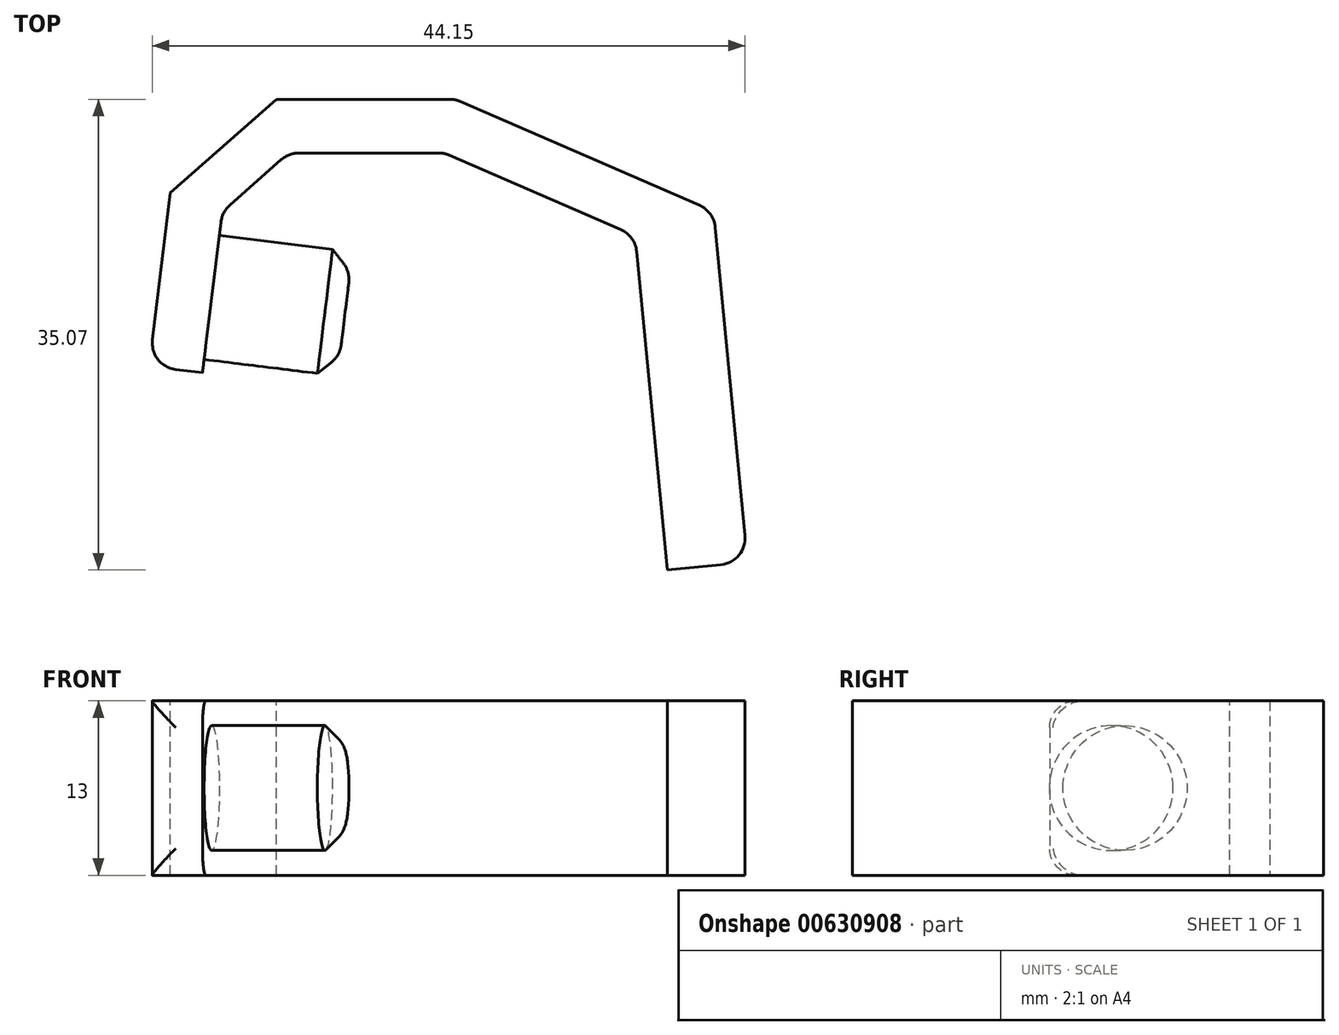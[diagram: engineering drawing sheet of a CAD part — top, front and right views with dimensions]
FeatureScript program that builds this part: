
annotation { "Feature Type Name" : "Feature", "Feature Type Description" : "" }
export const myFeature = defineFeature(function(context is Context, id is Id, definition is map)
    precondition{}
    {
        {
            var Q0;
            Q0=qCreatedBy(makeId("Top.planeOp"),FACE);
            var sketch = newSketch(context, id + "F0", { "sketchPlane" : qUnion([Q0])});
            skLineSegment(sketch, "E0", {"start": v(-44.74, -5.73) * mm, "end": v(-42.73, 10.65) * mm});
            skLineSegment(sketch, "E1", {"start": v(-42.73, 10.65) * mm, "end": v(-26.73, 10.65) * mm});
            skLineSegment(sketch, "E2", {"start": v(-26.73, 10.65) * mm, "end": v(-12.51, 4.47) * mm});
            skLineSegment(sketch, "E3.0", {"start": v(-25.9, 14.65) * mm, "end": v(-6.66, 6.28) * mm});
            skLineSegment(sketch, "E3.1", {"start": v(-46.27, 14.65) * mm, "end": v(-25.9, 14.65) * mm});
            skLineSegment(sketch, "E3.2", {"start": v(-48.7, -5.24) * mm, "end": v(-46.27, 14.65) * mm});
            skLineSegment(sketch, "E4", {"start": v(-48.7, -5.24) * mm, "end": v(-44.74, -5.73) * mm});
            skLineSegment(sketch, "E5", {"start": v(-12.51, 4.47) * mm, "end": v(-10.12, -20.42) * mm});
            skLineSegment(sketch, "E6", {"start": v(-6.66, 6.28) * mm, "end": v(-4.15, -19.84) * mm});
            skLineSegment(sketch, "E7", {"start": v(-4.15, -19.84) * mm, "end": v(-10.12, -20.42) * mm});
            skSolve(sketch);
        }
        {
            var Q0;
            Q0 = qSketchRegion(id + "F0", true);
            extrude(context, id + "F1", {"entities" : qUnion([Q0]), "depth" : 13 * mm, "offsetDistance" : 25 * mm});
        }
        {
            var Q0;
            Q0=makeQuery(id+"F1.opExtrude","SWEPT_FACE",FACE,{"disambiguationData":[OSD([sQuery(id+"F0.wireOp",EDGE,"E0")])]});
            var sketch = newSketch(context, id + "F2", { "sketchPlane" : qUnion([Q0])});
            skCircle(sketch, "E8", {"center": v(-5.5, 6.5) * mm, "radius": 4.65 * mm});
            skSolve(sketch);
        }
        {
            var Q0;
            Q0 = qSketchRegion(id + "F2", true);
            extrude(context, id + "F3", {"entities" : qUnion([Q0]), "operationType" : NewBodyOperationType.ADD, "depth" : 10 * mm, "offsetDistance" : 25 * mm});
        }
        {
            var Q0;
            Q0=makeQuery(id+"F3.opExtrude","CAP_EDGE",EDGE,{"disambiguationData":[OSD([sQuery(id+"F2.wireOp",EDGE,"E8")])],"isStart":false});
            chamfer(context, id + "F4", {"entities" : qUnion([Q0]), "width" : 1.5 * mm, "tangentPropagation" : true});
        }
        {
            var Q0;
            Q0=makeQuery(id+"F1.opExtrude","SWEPT_EDGE",EDGE,{"disambiguationData":[OSD([sQuery(id+"F0.wireOp",EDGE,"E0"),sQuery(id+"F0.wireOp",EDGE,"E1")])]});
            chamfer(context, id + "F5", {"entities" : qUnion([Q0]), "width" : 5 * mm, "tangentPropagation" : true});
        }
        {
            var Q0;
            Q0=makeQuery(id+"F1.opExtrude","CAP_FACE",FACE,{"disambiguationData":[OSD([sQuery(id+"F0.wireOp",EDGE,"E0"),sQuery(id+"F0.wireOp",EDGE,"E1"),sQuery(id+"F0.wireOp",EDGE,"E2"),sQuery(id+"F0.wireOp",EDGE,"E3.0"),sQuery(id+"F0.wireOp",EDGE,"E3.1"),sQuery(id+"F0.wireOp",EDGE,"E3.2"),sQuery(id+"F0.wireOp",EDGE,"E4"),sQuery(id+"F0.wireOp",EDGE,"N3BcXGvI-HXC5-peAH-YZqd-A4wPKsLQrxSF")])],"isStart":false});
            var sketch = newSketch(context, id + "F6", { "sketchPlane" : qUnion([Q0])});
            skLineSegment(sketch, "E9", {"start": v(-47.12, 7.68) * mm, "end": v(-39.24, 14.65) * mm});
            skLineSegment(sketch, "E10", {"start": v(-39.24, 14.65) * mm, "end": v(-43.87, 19.87) * mm});
            skLineSegment(sketch, "E11", {"start": v(-43.87, 19.87) * mm, "end": v(-51.8, 12.85) * mm});
            skLineSegment(sketch, "E12", {"start": v(-51.8, 12.85) * mm, "end": v(-47.12, 7.68) * mm});
            skSolve(sketch);
        }
        {
            var Q0;
            Q0 = qSketchRegion(id + "F6", true);
            extrude(context, id + "F7", {"entities" : qUnion([Q0]), "operationType" : NewBodyOperationType.REMOVE, "oppositeDirection" : true, "depth" : 25 * mm, "offsetDistance" : 25 * mm});
        }
        {
            var Q0;
            Q0=makeQuery(id+"F1.opExtrude","CAP_EDGE",EDGE,{"disambiguationData":[OSD([sQuery(id+"F0.wireOp",EDGE,"E4")])],"isStart":true});
            var Q1;
            Q1=makeQuery(id+"F1.opExtrude","CAP_EDGE",EDGE,{"disambiguationData":[OSD([sQuery(id+"F0.wireOp",EDGE,"E4")])],"isStart":false});
            var Q2;
            Q2=makeQuery(id+"F1.opExtrude","SWEPT_EDGE",EDGE,{"disambiguationData":[OSD([sQuery(id+"F0.wireOp",EDGE,"E6"),sQuery(id+"F0.wireOp",EDGE,"E7")])]});
            var Q3;
            Q3=makeQuery(id+"F3.opExtrude","CAP_EDGE",EDGE,{"disambiguationData":[OSD([sQuery(id+"F2.wireOp",EDGE,"E8")])],"isStart":true});
            var Q4;
            {var subQ0=sQuery(id+"F0.wireOp",EDGE,"E0");Q4=makeQuery(id+"F5.opChamfer","BLEND_EDGE",EDGE,{"blendedFrom":[makeQuery(id+"F1.opExtrude","SWEPT_EDGE",EDGE,{"disambiguationData":[OSD([subQ0,sQuery(id+"F0.wireOp",EDGE,"E1")])]}),makeQuery(id+"F1.opExtrude","SWEPT_FACE",FACE,{"disambiguationData":[OSD([subQ0])]})],"blendedInto":[makeQuery(id+"F1.opExtrude","SWEPT_FACE",FACE,{"disambiguationData":[OSD([subQ0])]})]});}
            var Q5;
            {var subQ0=sQuery(id+"F0.wireOp",EDGE,"E1");Q5=makeQuery(id+"F5.opChamfer","BLEND_EDGE",EDGE,{"blendedFrom":[makeQuery(id+"F1.opExtrude","SWEPT_EDGE",EDGE,{"disambiguationData":[OSD([sQuery(id+"F0.wireOp",EDGE,"E0"),subQ0])]}),makeQuery(id+"F1.opExtrude","SWEPT_FACE",FACE,{"disambiguationData":[OSD([subQ0])]})],"blendedInto":[makeQuery(id+"F1.opExtrude","SWEPT_FACE",FACE,{"disambiguationData":[OSD([subQ0])]})]});}
            var Q6;
            Q6=makeQuery(id+"F1.opExtrude","SWEPT_EDGE",EDGE,{"disambiguationData":[OSD([sQuery(id+"F0.wireOp",EDGE,"E1"),sQuery(id+"F0.wireOp",EDGE,"E2")])]});
            var Q7;
            Q7=makeQuery(id+"F1.opExtrude","SWEPT_EDGE",EDGE,{"disambiguationData":[OSD([sQuery(id+"F0.wireOp",EDGE,"E2"),sQuery(id+"F0.wireOp",EDGE,"E5")])]});
            var Q8;
            Q8=makeQuery(id+"F1.opExtrude","SWEPT_EDGE",EDGE,{"disambiguationData":[OSD([sQuery(id+"F0.wireOp",EDGE,"E3.0"),sQuery(id+"F0.wireOp",EDGE,"E6")])]});
            var Q9;
            Q9=makeQuery(id+"F1.opExtrude","SWEPT_EDGE",EDGE,{"disambiguationData":[OSD([sQuery(id+"F0.wireOp",EDGE,"E3.0"),sQuery(id+"F0.wireOp",EDGE,"E3.1")])]});
            var Q10;
            Q10=makeQuery(id+"F7.boolean.opBoolean","COPY",EDGE,{"derivedFrom":makeQuery(id+"F7.opExtrude","SWEPT_EDGE",EDGE,{"disambiguationData":[OSD([sQuery(id+"F0.wireOp",EDGE,"E3.1"),sQuery(id+"F6.wireOp",EDGE,"E9"),sQuery(id+"F6.wireOp",EDGE,"E10")])]})});
            var Q11;
            Q11=makeQuery(id+"F7.boolean.opBoolean","COPY",EDGE,{"derivedFrom":makeQuery(id+"F7.opExtrude","SWEPT_EDGE",EDGE,{"disambiguationData":[OSD([sQuery(id+"F0.wireOp",EDGE,"E3.2"),sQuery(id+"F6.wireOp",EDGE,"E9"),sQuery(id+"F6.wireOp",EDGE,"E12")])]})});
            var Q12;
            Q12=makeQuery(id+"F1.opExtrude","SWEPT_EDGE",EDGE,{"disambiguationData":[OSD([sQuery(id+"F0.wireOp",EDGE,"E3.2"),sQuery(id+"F0.wireOp",EDGE,"E4")])]});
            var Q13;
            {var subQ0=sQuery(id+"F2.wireOp",EDGE,"E8");Q13=makeQuery(id+"F4.opChamfer","BLEND_EDGE",EDGE,{"blendedFrom":[makeQuery(id+"F3.opExtrude","CAP_EDGE",EDGE,{"disambiguationData":[OSD([subQ0])],"isStart":false}),makeQuery(id+"F3.opExtrude","CAP_FACE",FACE,{"disambiguationData":[OSD([subQ0])],"isStart":false})],"blendedInto":[makeQuery(id+"F3.opExtrude","CAP_FACE",FACE,{"disambiguationData":[OSD([subQ0])],"isStart":false})]});}
            fillet(context, id + "F8", {"entities" : qUnion([Q0, Q1, Q2, Q3, Q4, Q5, Q6, Q7, Q8, Q9, Q10, Q11, Q12, Q13]), "radius" : 2 * mm, "tangentPropagation" : true, "allowEdgeOverflow" : false});
        }
    });
